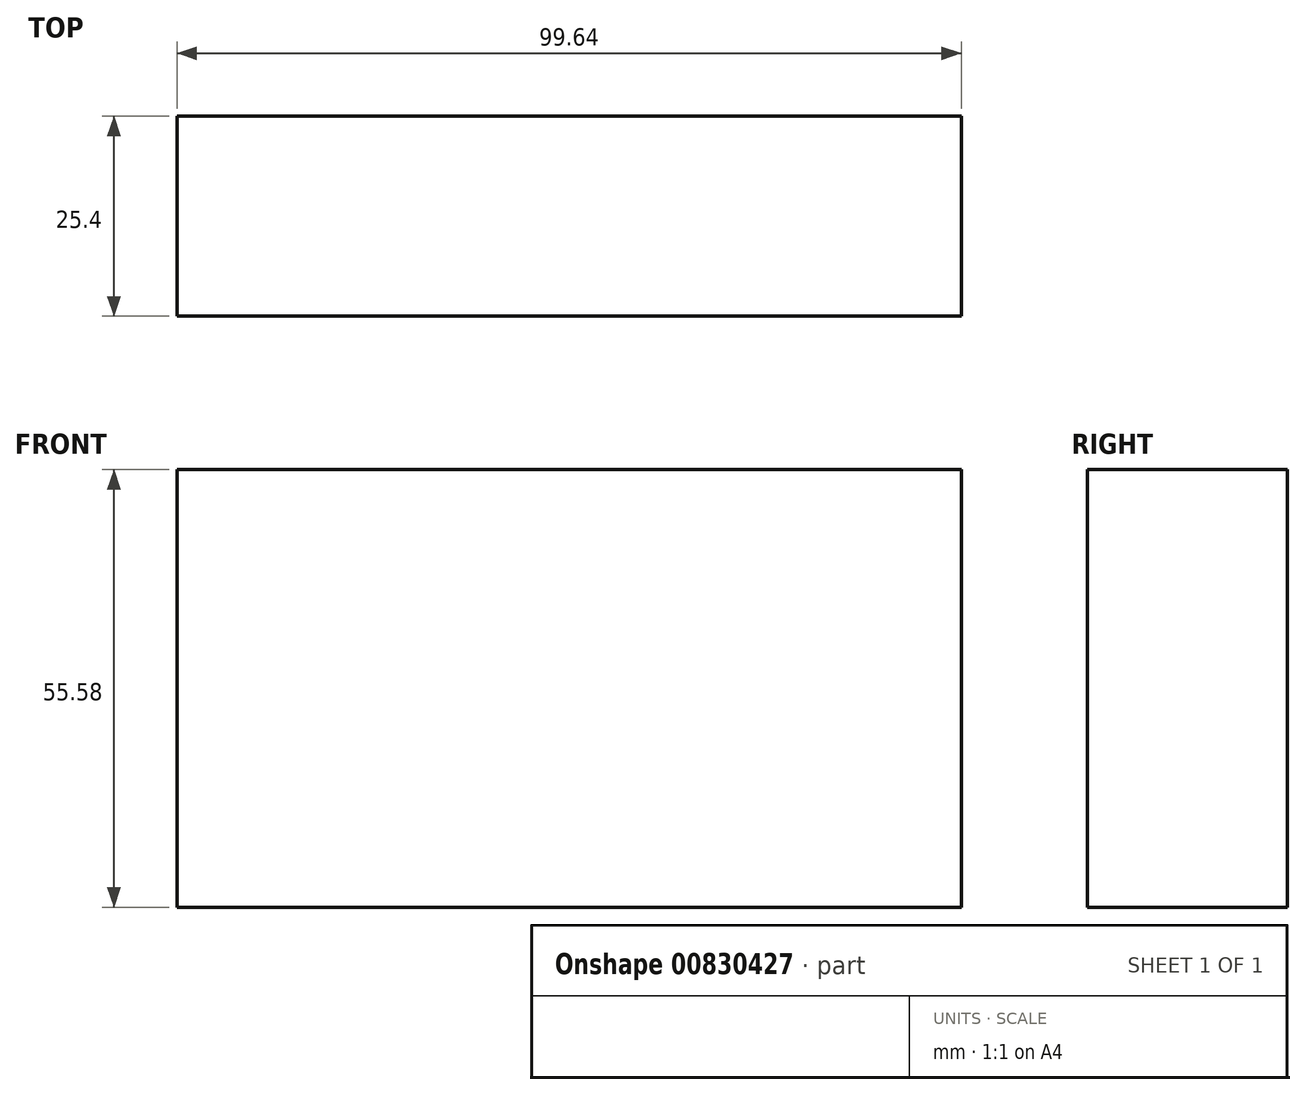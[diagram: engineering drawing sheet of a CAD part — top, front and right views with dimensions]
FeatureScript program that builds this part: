
annotation { "Feature Type Name" : "Feature", "Feature Type Description" : "" }
export const myFeature = defineFeature(function(context is Context, id is Id, definition is map)
    precondition{}
    {
        {
            var Q0;
            Q0=qCreatedBy(makeId("Front.planeOp"),FACE);
            var sketch = newSketch(context, id + "F0", { "sketchPlane" : qUnion([Q0])});
            skLineSegment(sketch, "E0.bottom", {"start": v(0, 0) * mm, "end": v(99.64, 0) * mm});
            skLineSegment(sketch, "E0.top", {"start": v(0, 55.58) * mm, "end": v(99.64, 55.58) * mm});
            skLineSegment(sketch, "E0.left", {"start": v(0, 0) * mm, "end": v(0, 55.58) * mm});
            skLineSegment(sketch, "E0.right", {"start": v(99.64, 0) * mm, "end": v(99.64, 55.58) * mm});
            skSolve(sketch);
        }
        {
            var Q0;
            Q0=makeQuery(id+"F0.imprint","IMPRINT",FACE,{"disambiguationData":[TD([[makeQuery(id+"F0.imprint","IMPRINT",EDGE,{"derivedFrom":sQuery(id+"F0.wireOp",EDGE,"E0.bottom")}),1.0]])]});
            extrude(context, id + "F1", {"entities" : qUnion([Q0]), "oppositeDirection" : true, "depth" : 25.4 * mm, "offsetDistance" : 25.4 * mm});
        }
    });
